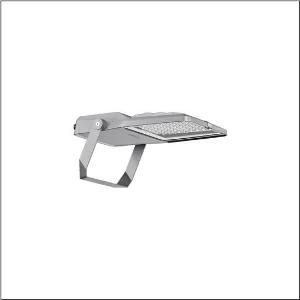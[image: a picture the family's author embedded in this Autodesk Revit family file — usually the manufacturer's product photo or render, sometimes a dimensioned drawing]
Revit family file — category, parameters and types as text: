
# Revit family: floodlight_fl_21_iq_mini___pl33t_5xa7772c4f1a_48c1
name_source: partatom
category: Lighting Fixtures
units: mm (PartAtom-declared; Revit-internal decimal feet)

## family parameters
Cut with Voids When Loaded = No
Host = Face
Light Source = No
Part Type = Normal
Room Calculation Point = No
Round Connector Dimension = Use Diameter
Shared = No

## types (1)
- --- (1 x LED, 12570 lm, 87.2 W, 4000K)
    Apparent Load = 87 VA
    CIE Flux Codes = 26 75 99 100 100
    Color Rendering = 70
    Color Temperature = 4000K
    Default Elevation = 1800 mm
    Description = Floodlight FL 21 iQ mini, floodlight, primary light control with lens, of PMMA, primary optical cover: protective disc, of toughened safety glass, transparent, light distribution: PL33T, light emission: direct distribution, installation type: surface-mounted, lamps: LED, High Power LED, rated values: 12.570lm | 87,2W | 144,2lm/W (begin service life); end service life: 12.570lm | 92,1W; at 50% lumin. flux: 6.285lm | 40,2W | 156,3lm/W, colour temperature: 4000K, colour rendering: CRI > 70, light colour: 740, light setting 1 begin service life: 100% | 12.570lm | 87,2W | 144,2lm/W | 4.000K, light setting 1 end service life: 92,1W, further light settings possible, control: Street-Remote, Auto-Match, Temp-Guard, Night-Set, Smart-Wire, Desk-Remote (wireless, voltage-free reading and setting of iQ features in the workshop via application-optimized NFC function/RFID function), optimised constant luminous flux control (CLO 2.0), pre-setting: linear dimming characteristic, with terminal, 6-pole, mains connection: 220..240V, AC, 50/60Hz, luminaire housing, of diecast aluminium, powder-coated, SITECO metallic grey (DB 702S), corrosivity category C5 mid according to DIN EN ISO 12944suitable for swimming poolschlorine-resistant, sealing non-destructively replaceable, mounting bracket, of steel, galvanised, powder-coated, SITECO metallic grey (DB 702S), protection rating (complete): IP66, insulation class (complete): insulation class II (safety insulation), certification: CE, ENEC, VDE, protection symbol: D, impact resistance: IK08, permissible operating ambient temperature: -40..+40°C, permissible operating ambient temperature for outdoor applications: -40..+50°C, standard: DIN EN 12944, LABS conformity tested according to VDMA 24364:2018-05, packaging unit: 1 piece

Light Distribution: PL33T
    Height = 70 mm
    Lamp = 1 x LED
    Lamp Light Flux = 12570 lm
    Lamp Power = 87.2 W
    Lamp count = 1
    Length = 485 mm
    Luminous efficacy = 144 lm/W
    Manufacturer = Siteco
    ModVariant = No
    Model = 5XA7772C4F1A
    Mounting Place = Pole
    Mounting Type = Pole annexe
    Number of Poles = 1
    OnlyDefault = Yes
    Power Factor = 1
    Product Name = Floodlight FL 21 iQ mini | PL33T
    Product group = floodlight | pylon annexe
    ProductGroupID = 6201
    Protection Class = Protection class II
    Protection Degree = IP 66
    RLX_Detail_Level = 1
    RLX_Emergency_Light_Flux = 0 lm
    RLX_Emergency_Type = 0
    RLX_Emergency_Type_DB = No
    RlxData = <blob elided: 96465 chars, md5=a55088e7>
    Socket = socket
    Standby Power = 0 W
    System Light Flux = 12570 lm
    System Power = 87 W
    Type Comments = factory setting: luminous flux: 100 % | dim-lin: 254 | 456 mA
    Type Image = l_1006845.jpg
    URL = http://relux.com
    VarID = @adj_150471
    Voltage = 0 V
    Weight = 0.00 kg
    Width = 337 mm

## geometry (parser evidence)
native form markers: Blend x4, Sweep x10
no freeform markers — native parametric forms only
